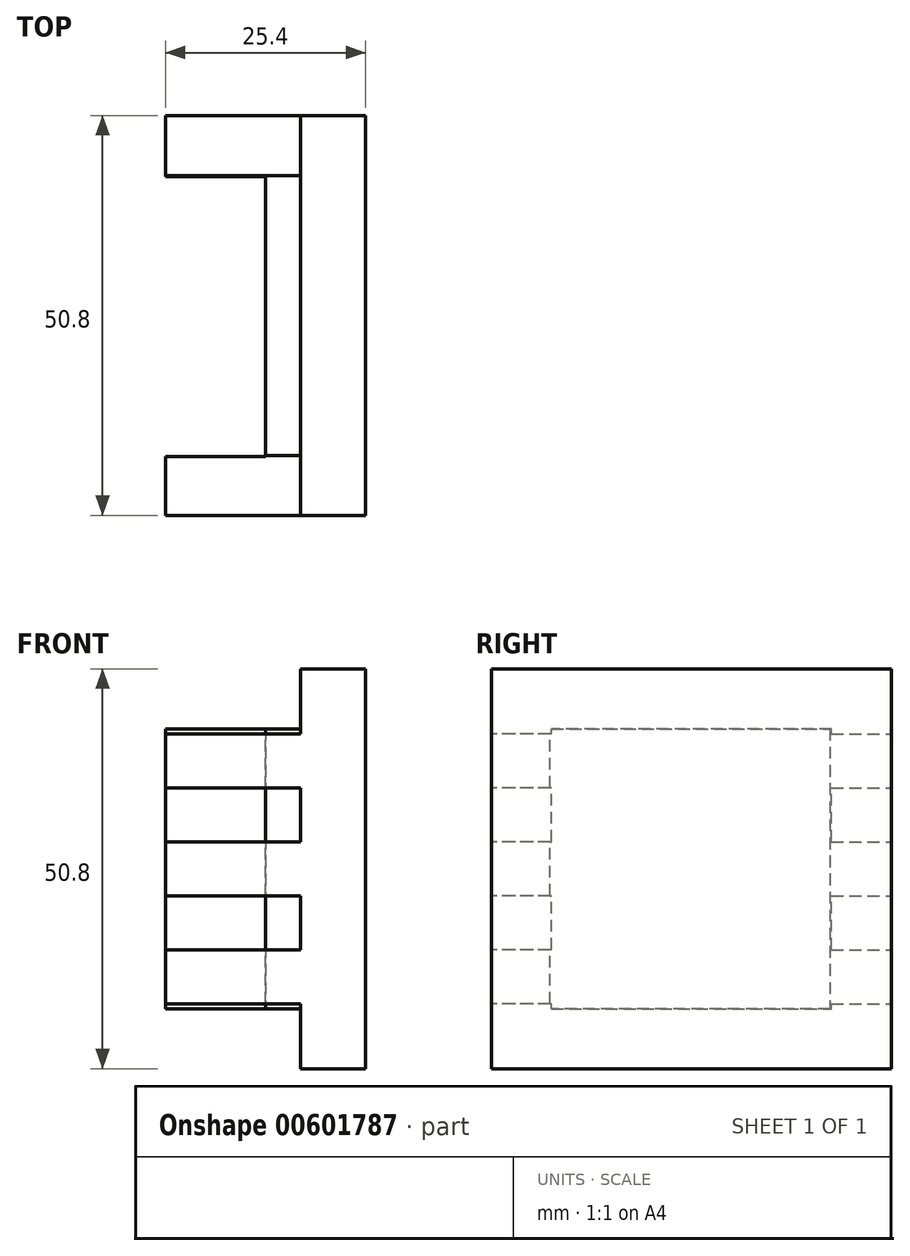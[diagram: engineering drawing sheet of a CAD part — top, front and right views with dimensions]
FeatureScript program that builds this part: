
annotation { "Feature Type Name" : "Feature", "Feature Type Description" : "" }
export const myFeature = defineFeature(function(context is Context, id is Id, definition is map)
    precondition{}
    {
        {
            var Q0;
            Q0=qCreatedBy(makeId("Front.planeOp"),FACE);
            var sketch = newSketch(context, id + "F0", { "sketchPlane" : qUnion([Q0])});
            skLineSegment(sketch, "E0.bottom", {"start": v(0, 0) * mm, "end": v(25.4, 0) * mm});
            skLineSegment(sketch, "E0.top", {"start": v(0, 50.8) * mm, "end": v(25.4, 50.8) * mm});
            skLineSegment(sketch, "E0.left", {"start": v(0, 0) * mm, "end": v(0, 50.8) * mm});
            skLineSegment(sketch, "E0.right", {"start": v(25.4, 0) * mm, "end": v(25.4, 50.8) * mm});
            skSolve(sketch);
        }
        {
            var Q0;
            Q0=makeQuery(id+"F0.imprint","IMPRINT",FACE,{"disambiguationData":[TD([[makeQuery(id+"F0.imprint","IMPRINT",EDGE,{"derivedFrom":sQuery(id+"F0.wireOp",EDGE,"E0.bottom")}),1.0]])]});
            extrude(context, id + "F1", {"entities" : qUnion([Q0]), "depth" : 50.8 * mm, "offsetDistance" : 25.4 * mm});
        }
        {
            var Q0;
            Q0=makeQuery(id+"F1.opExtrude","SWEPT_FACE",FACE,{"disambiguationData":[OSD([sQuery(id+"F0.wireOp",EDGE,"E0.left")])]});
            var sketch = newSketch(context, id + "F2", { "sketchPlane" : qUnion([Q0])});
            skLineSegment(sketch, "E1", {"start": v(7.8, 43.18) * mm, "end": v(7.8, 7.62) * mm});
            skLineSegment(sketch, "E2", {"start": v(7.8, 7.62) * mm, "end": v(43.36, 7.62) * mm});
            skLineSegment(sketch, "E3", {"start": v(43.36, 7.62) * mm, "end": v(43.36, 43.18) * mm});
            skLineSegment(sketch, "E4", {"start": v(43.36, 43.18) * mm, "end": v(7.8, 43.18) * mm});
            skSolve(sketch);
        }
        {
            var Q0;
            Q0=makeQuery(id+"F2.imprint","IMPRINT",FACE,{"disambiguationData":[TD([[makeQuery(id+"F2.imprint","IMPRINT",EDGE,{"derivedFrom":sQuery(id+"F2.wireOp",EDGE,"E1")}),1.0]])]});
            extrude(context, id + "F3", {"entities" : qUnion([Q0]), "operationType" : NewBodyOperationType.REMOVE, "oppositeDirection" : true, "depth" : 12.7 * mm, "offsetDistance" : 25.4 * mm});
        }
        {
            var Q0;
            Q0=makeQuery(id+"F1.opExtrude","CAP_FACE",FACE,{"disambiguationData":[OSD([sQuery(id+"F0.wireOp",EDGE,"E0.bottom"),sQuery(id+"F0.wireOp",EDGE,"E0.top"),sQuery(id+"F0.wireOp",EDGE,"E0.left"),sQuery(id+"F0.wireOp",EDGE,"E0.right")])],"isStart":true});
            var sketch = newSketch(context, id + "F4", { "sketchPlane" : qUnion([Q0])});
            skLineSegment(sketch, "E5", {"start": v(0, 50.8) * mm, "end": v(-17.15, 50.8) * mm});
            skLineSegment(sketch, "E6", {"start": v(-17.15, 50.8) * mm, "end": v(-17.15, 42.55) * mm});
            skLineSegment(sketch, "E7", {"start": v(-17.15, 42.55) * mm, "end": v(0, 42.55) * mm});
            skLineSegment(sketch, "E8", {"start": v(0, 42.55) * mm, "end": v(0, 50.8) * mm});
            skLineSegment(sketch, "E9", {"start": v(0, 35.69) * mm, "end": v(-17.15, 35.69) * mm});
            skLineSegment(sketch, "E10", {"start": v(-17.15, 35.69) * mm, "end": v(-17.15, 28.83) * mm});
            skLineSegment(sketch, "E11", {"start": v(-17.15, 28.83) * mm, "end": v(0, 28.83) * mm});
            skLineSegment(sketch, "E12", {"start": v(0, 28.83) * mm, "end": v(0, 35.69) * mm});
            skLineSegment(sketch, "E13", {"start": v(0, 0) * mm, "end": v(-17.15, 0) * mm});
            skLineSegment(sketch, "E14", {"start": v(-17.15, 0) * mm, "end": v(-17.15, 8.26) * mm});
            skLineSegment(sketch, "E15", {"start": v(-17.15, 8.26) * mm, "end": v(0, 8.26) * mm});
            skLineSegment(sketch, "E16", {"start": v(0, 8.26) * mm, "end": v(0, 0) * mm});
            skLineSegment(sketch, "E17", {"start": v(0, 21.97) * mm, "end": v(-17.15, 21.97) * mm});
            skLineSegment(sketch, "E18", {"start": v(-17.15, 21.97) * mm, "end": v(-17.15, 15.11) * mm});
            skLineSegment(sketch, "E19", {"start": v(-17.15, 15.11) * mm, "end": v(0, 15.11) * mm});
            skLineSegment(sketch, "E20", {"start": v(0, 15.11) * mm, "end": v(0, 21.97) * mm});
            skSolve(sketch);
        }
        {
            var Q0;
            Q0=makeQuery(id+"F4.imprint","IMPRINT",FACE,{"disambiguationData":[TD([[makeQuery(id+"F4.imprint","IMPRINT",EDGE,{"derivedFrom":sQuery(id+"F4.wireOp",EDGE,"E5")}),1.0]])]});
            var Q1;
            Q1=makeQuery(id+"F4.imprint","IMPRINT",FACE,{"disambiguationData":[TD([[makeQuery(id+"F4.imprint","IMPRINT",EDGE,{"derivedFrom":sQuery(id+"F4.wireOp",EDGE,"E9")}),1.0]])]});
            var Q2;
            Q2=makeQuery(id+"F4.imprint","IMPRINT",FACE,{"disambiguationData":[TD([[makeQuery(id+"F4.imprint","IMPRINT",EDGE,{"derivedFrom":sQuery(id+"F4.wireOp",EDGE,"E17")}),1.0]])]});
            var Q3;
            Q3=makeQuery(id+"F4.imprint","IMPRINT",FACE,{"disambiguationData":[TD([[makeQuery(id+"F4.imprint","IMPRINT",EDGE,{"derivedFrom":sQuery(id+"F4.wireOp",EDGE,"E13")}),-1.0]])]});
            extrude(context, id + "F5", {"entities" : qUnion([Q0, Q1, Q2, Q3]), "operationType" : NewBodyOperationType.REMOVE, "oppositeDirection" : true, "depth" : 7.62 * mm, "offsetDistance" : 25.4 * mm});
        }
        {
            var Q0;
            Q0=makeQuery(id+"F1.opExtrude","CAP_FACE",FACE,{"disambiguationData":[OSD([sQuery(id+"F0.wireOp",EDGE,"E0.bottom"),sQuery(id+"F0.wireOp",EDGE,"E0.top"),sQuery(id+"F0.wireOp",EDGE,"E0.left"),sQuery(id+"F0.wireOp",EDGE,"E0.right")])],"isStart":false});
            var sketch = newSketch(context, id + "F6", { "sketchPlane" : qUnion([Q0])});
            skLineSegment(sketch, "E21", {"start": v(0, 42.55) * mm, "end": v(17.14, 42.55) * mm});
            skLineSegment(sketch, "E22", {"start": v(17.14, 42.55) * mm, "end": v(17.14, 50.8) * mm});
            skLineSegment(sketch, "E23", {"start": v(17.14, 50.8) * mm, "end": v(0, 50.8) * mm});
            skLineSegment(sketch, "E24", {"start": v(0, 50.8) * mm, "end": v(0, 42.55) * mm});
            skLineSegment(sketch, "E25", {"start": v(0, 35.69) * mm, "end": v(17.14, 35.69) * mm});
            skLineSegment(sketch, "E26", {"start": v(17.14, 35.69) * mm, "end": v(17.14, 28.83) * mm});
            skLineSegment(sketch, "E27", {"start": v(17.14, 28.83) * mm, "end": v(0, 28.83) * mm});
            skLineSegment(sketch, "E28", {"start": v(0, 28.83) * mm, "end": v(0, 35.69) * mm});
            skLineSegment(sketch, "E29", {"start": v(17.14, 21.97) * mm, "end": v(0, 21.97) * mm});
            skLineSegment(sketch, "E30", {"start": v(0, 21.97) * mm, "end": v(0, 15.11) * mm});
            skLineSegment(sketch, "E31", {"start": v(0, 15.11) * mm, "end": v(17.14, 15.11) * mm});
            skLineSegment(sketch, "E32", {"start": v(17.14, 15.11) * mm, "end": v(17.14, 21.97) * mm});
            skLineSegment(sketch, "E33", {"start": v(17.14, 8.25) * mm, "end": v(17.14, 0) * mm});
            skLineSegment(sketch, "E34", {"start": v(17.14, 0) * mm, "end": v(0, 0) * mm});
            skLineSegment(sketch, "E35", {"start": v(0, 0) * mm, "end": v(0, 8.25) * mm});
            skLineSegment(sketch, "E36", {"start": v(0, 8.25) * mm, "end": v(17.14, 8.25) * mm});
            skSolve(sketch);
        }
        {
            var Q0;
            Q0 = qSketchRegion(id + "F6", true);
            extrude(context, id + "F7", {"entities" : qUnion([Q0]), "operationType" : NewBodyOperationType.REMOVE, "oppositeDirection" : true, "depth" : 7.62 * mm, "offsetDistance" : 25.4 * mm});
        }
        {
            var Q0;
            Q0=makeQuery(id+"F1.opExtrude","SWEPT_FACE",FACE,{"disambiguationData":[OSD([sQuery(id+"F0.wireOp",EDGE,"E0.top")])]});
            var sketch = newSketch(context, id + "F8", { "sketchPlane" : qUnion([Q0])});
            skLineSegment(sketch, "E37", {"start": v(17.15, -7.62) * mm, "end": v(17.14, -43.18) * mm});
            skLineSegment(sketch, "E38", {"start": v(17.14, -43.18) * mm, "end": v(0, -43.18) * mm});
            skLineSegment(sketch, "E39", {"start": v(0, -43.18) * mm, "end": v(0, -7.62) * mm});
            skLineSegment(sketch, "E40", {"start": v(0, -7.62) * mm, "end": v(17.15, -7.62) * mm});
            skLineSegment(sketch, "E41", {"start": v(0, -43.18) * mm, "end": v(17.14, -43.18) * mm});
            skLineSegment(sketch, "E42", {"start": v(17.15, -7.62) * mm, "end": v(0, -7.62) * mm});
            skLineSegment(sketch, "E43", {"start": v(0, -7.62) * mm, "end": v(0, -43.18) * mm});
            skSolve(sketch);
        }
        {
            var Q0;
            Q0 = qSketchRegion(id + "F8", true);
            extrude(context, id + "F9", {"entities" : qUnion([Q0]), "operationType" : NewBodyOperationType.REMOVE, "oppositeDirection" : true, "depth" : 7.62 * mm, "offsetDistance" : 25.4 * mm});
        }
        {
            var Q0;
            Q0=makeQuery(id+"F1.opExtrude","SWEPT_FACE",FACE,{"disambiguationData":[OSD([sQuery(id+"F0.wireOp",EDGE,"E0.bottom")])]});
            var sketch = newSketch(context, id + "F10", { "sketchPlane" : qUnion([Q0])});
            skLineSegment(sketch, "E44", {"start": v(17.14, 43.18) * mm, "end": v(17.15, 7.62) * mm});
            skLineSegment(sketch, "E45", {"start": v(17.15, 7.62) * mm, "end": v(0, 7.62) * mm});
            skLineSegment(sketch, "E46", {"start": v(0, 7.62) * mm, "end": v(0, 43.18) * mm});
            skLineSegment(sketch, "E47", {"start": v(0, 43.18) * mm, "end": v(17.14, 43.18) * mm});
            skSolve(sketch);
        }
        {
            var Q0;
            Q0 = qSketchRegion(id + "F10", true);
            extrude(context, id + "F11", {"entities" : qUnion([Q0]), "operationType" : NewBodyOperationType.REMOVE, "oppositeDirection" : true, "depth" : 7.62 * mm, "offsetDistance" : 25.4 * mm});
        }
    });
